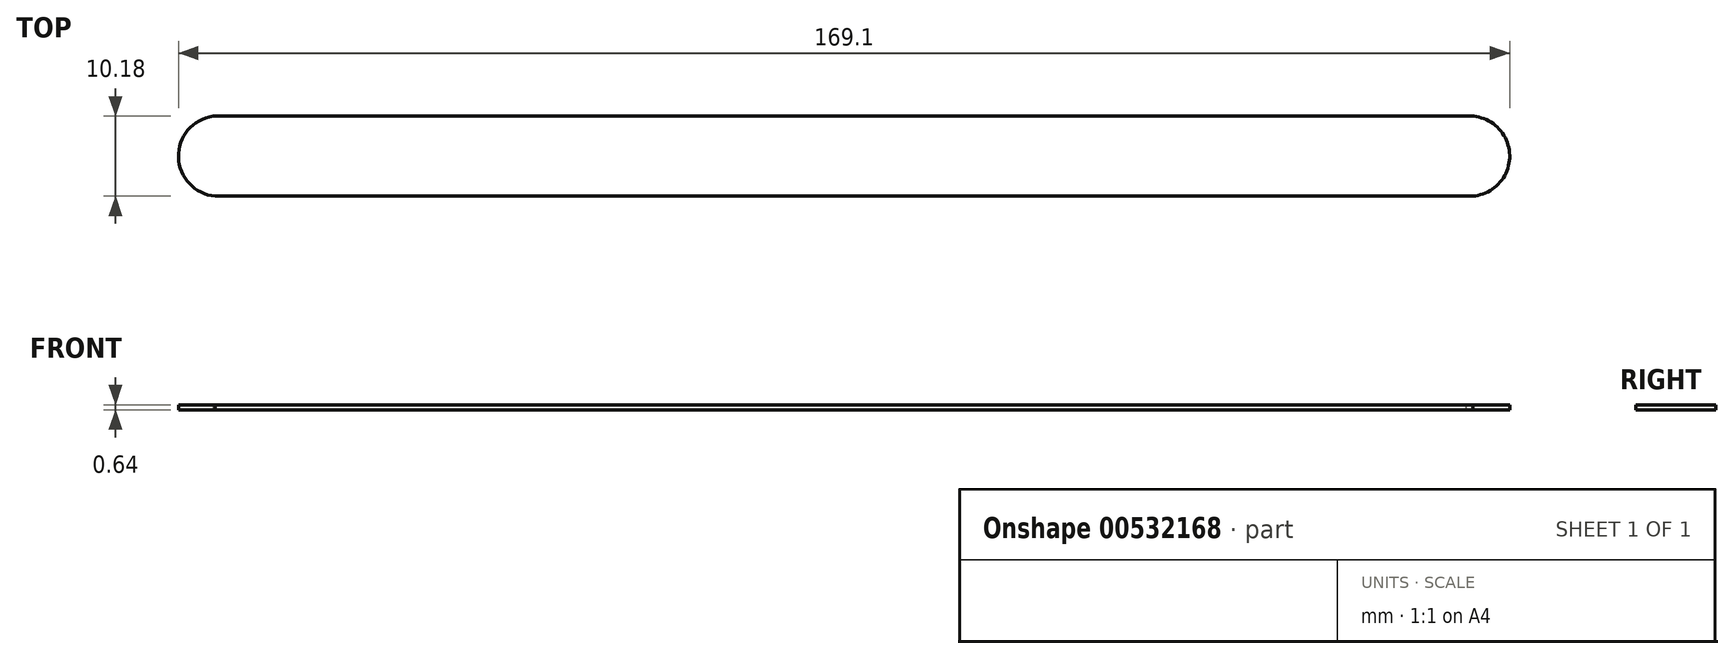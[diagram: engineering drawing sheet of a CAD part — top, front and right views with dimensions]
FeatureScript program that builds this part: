
annotation { "Feature Type Name" : "Feature", "Feature Type Description" : "" }
export const myFeature = defineFeature(function(context is Context, id is Id, definition is map)
    precondition{}
    {
        {
            var Q0;
            Q0=qCreatedBy(makeId("Top.planeOp"),FACE);
            var sketch = newSketch(context, id + "F0", { "sketchPlane" : qUnion([Q0])});
            skLineSegment(sketch, "E0.bottom", {"start": v(80.6, -5.08) * mm, "end": v(-79.14, -5.08) * mm});
            skLineSegment(sketch, "E0.top", {"start": v(80.64, 5.08) * mm, "end": v(-79.43, 5.08) * mm});
            skPoint(sketch, "E0.middle", {"position": v(0, 0) * mm});
            skArc(sketch, "E1", {"start": v(80.6, -5.08) * mm, "mid": v(85.26, 0.44) * mm, "end": v(79.72, 5.08) * mm});
            skArc(sketch, "E2", {"start": v(-79.43, 5.08) * mm, "mid": v(-83.82, -0.13) * mm, "end": v(-79.14, -5.08) * mm});
            skPoint(sketch, "E3.orphan", {"position": v(-86.36, 5.08) * mm});
            skPoint(sketch, "E4.orphan", {"position": v(-86.36, -5.08) * mm});
            skPoint(sketch, "E0.left.start.orphan", {"position": v(86.36, -5.08) * mm});
            skPoint(sketch, "E5.orphan", {"position": v(86.36, 5.08) * mm});
            skSolve(sketch);
        }
        {
            var Q0;
            Q0 = qSketchRegion(id + "F0", true);
            extrude(context, id + "F1", {"entities" : qUnion([Q0]), "depth" : 0.64 * mm, "offsetDistance" : 25.4 * mm});
        }
    });
